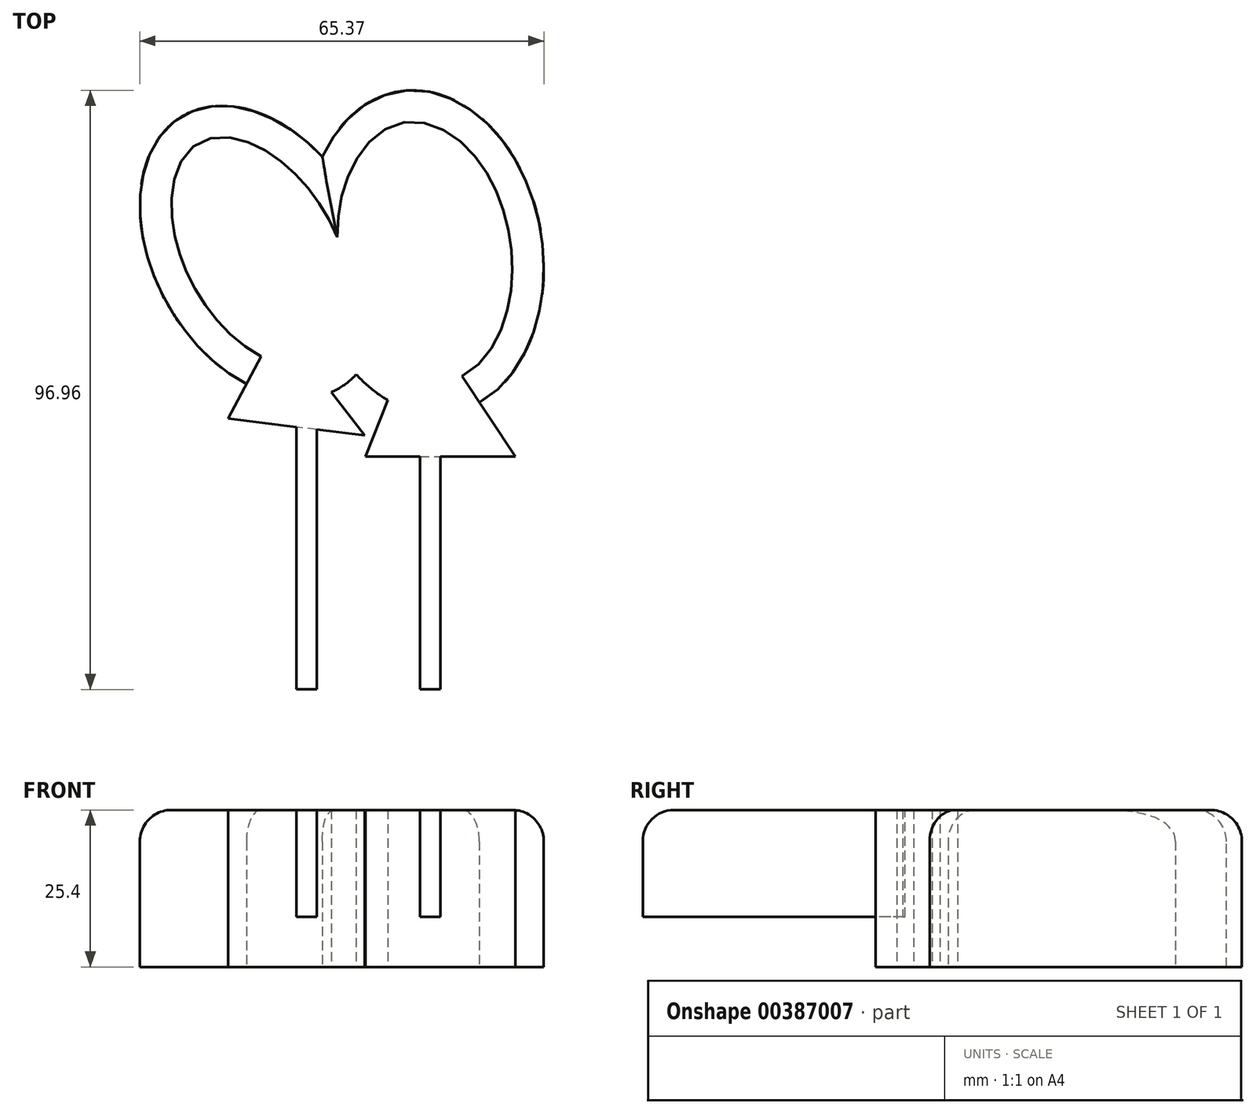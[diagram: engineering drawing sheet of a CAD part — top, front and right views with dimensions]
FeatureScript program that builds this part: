
annotation { "Feature Type Name" : "Feature", "Feature Type Description" : "" }
export const myFeature = defineFeature(function(context is Context, id is Id, definition is map)
    precondition{}
    {
        {
            var Q0;
            Q0=qCreatedBy(makeId("Top.planeOp"),FACE);
            var sketch = newSketch(context, id + "F0", { "sketchPlane" : qUnion([Q0])});
            skEllipse(sketch, "E0", {"center": v(0, 0) * mm, "majorRadius": 25.4 * mm, "minorRadius": 17.28 * mm, "majorAxis": v(-0.5, 0.87)});
            skLineSegment(sketch, "E1", {"start": v(-2.33, -21.36) * mm, "end": v(-5.27, -26.95) * mm});
            skLineSegment(sketch, "E2", {"start": v(11.43, -22.64) * mm, "end": v(16.8, -29.63) * mm});
            skLineSegment(sketch, "E3", {"start": v(16.8, -29.63) * mm, "end": v(-5.27, -26.95) * mm});
            skSolve(sketch);
        }
        {
            var Q0;
            Q0 = qSketchRegion(id + "F0", true);
            extrude(context, id + "F1", {"entities" : qUnion([Q0]), "depth" : 25.4 * mm});
        }
        {
            var Q0;
            Q0=qCreatedBy(makeId("Top.planeOp"),FACE);
            var sketch = newSketch(context, id + "F2", { "sketchPlane" : qUnion([Q0])});
            skEllipse(sketch, "E4", {"center": v(26.53, 0) * mm, "majorRadius": 26.34 * mm, "minorRadius": 19.05 * mm, "majorAxis": v(-0.15, 0.99)});
            skLineSegment(sketch, "E5", {"start": v(20.56, -23.96) * mm, "end": v(16.92, -33.1) * mm});
            skLineSegment(sketch, "E6", {"start": v(16.92, -33.1) * mm, "end": v(41.15, -33.1) * mm});
            skLineSegment(sketch, "E7", {"start": v(41.15, -33.1) * mm, "end": v(35.37, -24.35) * mm});
            skSolve(sketch);
        }
        {
            var Q0;
            Q0 = qSketchRegion(id + "F2", true);
            extrude(context, id + "F3", {"entities" : qUnion([Q0]), "operationType" : NewBodyOperationType.ADD, "depth" : 25.4 * mm});
        }
        {
            var Q0;
            Q0=makeQuery(id+"F3.boolean.opBoolean","MERGE",FACE,{"derivedFrom":[makeQuery(id+"F1.opExtrude","CAP_FACE",FACE,{"disambiguationData":[OSD([sQuery(id+"F0.wireOp",EDGE,"E0"),sQuery(id+"F0.wireOp",EDGE,"E1"),sQuery(id+"F0.wireOp",EDGE,"E2"),sQuery(id+"F0.wireOp",EDGE,"E3")])],"isStart":false}),makeQuery(id+"F3.opExtrude","CAP_FACE",FACE,{"disambiguationData":[OSD([sQuery(id+"F2.wireOp",EDGE,"E4"),sQuery(id+"F2.wireOp",EDGE,"E5"),sQuery(id+"F2.wireOp",EDGE,"E6"),sQuery(id+"F2.wireOp",EDGE,"E7")])],"isStart":false})]});
            var sketch = newSketch(context, id + "F4", { "sketchPlane" : qUnion([Q0])});
            skLineSegment(sketch, "E8.bottom", {"start": v(5.76, -28.3) * mm, "end": v(9.07, -28.3) * mm});
            skLineSegment(sketch, "E8.top", {"start": v(5.76, -70.77) * mm, "end": v(9.07, -70.77) * mm});
            skLineSegment(sketch, "E8.left", {"start": v(5.76, -28.3) * mm, "end": v(5.76, -70.77) * mm});
            skLineSegment(sketch, "E8.right", {"start": v(9.07, -28.3) * mm, "end": v(9.07, -70.77) * mm});
            skPoint(sketch, "E9.oppositeSnap0", {"position": v(29.04, -33.1) * mm});
            skLineSegment(sketch, "E9.bottom", {"start": v(25.74, -33.1) * mm, "end": v(29.04, -33.1) * mm});
            skLineSegment(sketch, "E9.top", {"start": v(25.74, -70.77) * mm, "end": v(29.04, -70.77) * mm});
            skLineSegment(sketch, "E9.left", {"start": v(25.74, -33.1) * mm, "end": v(25.74, -70.77) * mm});
            skLineSegment(sketch, "E9.right", {"start": v(29.04, -33.1) * mm, "end": v(29.04, -70.77) * mm});
            skSolve(sketch);
        }
        {
            var Q0;
            Q0 = qSketchRegion(id + "F4", true);
            extrude(context, id + "F5", {"entities" : qUnion([Q0]), "operationType" : NewBodyOperationType.ADD, "oppositeDirection" : true, "depth" : 17.27 * mm});
        }
        {
            var Q0;
            {var subQ0=sQuery(id+"F2.wireOp",EDGE,"E4");var subQ2=sQuery(id+"F2.wireOp",EDGE,"E7");Q0=makeQuery(id+"F3.boolean.opBoolean","SPLIT",EDGE,{"disambiguationData":[TD([makeQuery(id+"F3.opExtrude","SWEPT_FACE",FACE,{"disambiguationData":[OSD([subQ2])]})])],"derivedFrom":makeQuery(id+"F3.opExtrude","CAP_EDGE",EDGE,{"disambiguationData":[OSD([subQ0])],"isStart":false})});}
            var Q1;
            {var subQ1=sQuery(id+"F0.wireOp",EDGE,"E1");var subQ2=sQuery(id+"F0.wireOp",EDGE,"E0");Q1=makeQuery(id+"F3.boolean.opBoolean","SPLIT",EDGE,{"disambiguationData":[TD([makeQuery(id+"F1.opExtrude","SWEPT_FACE",FACE,{"disambiguationData":[OSD([subQ1])]})])],"derivedFrom":makeQuery(id+"F1.opExtrude","CAP_EDGE",EDGE,{"disambiguationData":[OSD([subQ2])],"isStart":false})});}
            var Q2;
            Q2=makeQuery(id+"F5.opExtrude","CAP_EDGE",EDGE,{"disambiguationData":[OSD([sQuery(id+"F4.wireOp",EDGE,"E8.top")])],"isStart":true});
            var Q3;
            Q3=makeQuery(id+"F5.opExtrude","CAP_EDGE",EDGE,{"disambiguationData":[OSD([sQuery(id+"F4.wireOp",EDGE,"E9.top")])],"isStart":true});
            fillet(context, id + "F6", {"entities" : qUnion([Q0, Q1, Q2, Q3]), "radius" : 5.08 * mm, "tangentPropagation" : true, "allowEdgeOverflow" : false});
        }
    });
